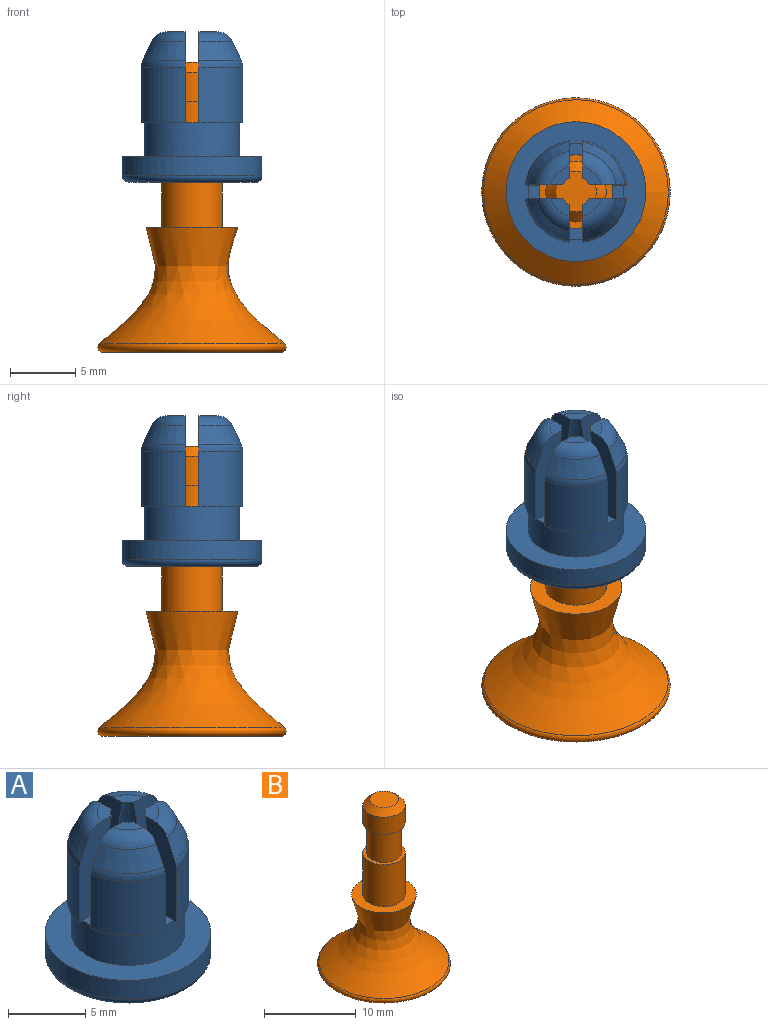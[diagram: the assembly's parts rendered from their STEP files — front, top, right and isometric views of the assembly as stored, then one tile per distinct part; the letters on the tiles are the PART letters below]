
ASSEMBLY  parts=2 mates=1
PART A: 50 faces, bbox 11.7x11.7x11.7 mm
  f0: torus R=2.67mm, axis (0,0,-1), area 2.8mm2, adj f7,f9,f12,f21
  f1: cone r=3.94mm half-angle=25.1deg, axis (0,0,-1), area 7.1mm2, adj f10,f41,f42,f47
  f2: torus R=1.99mm, axis (0,0,-1), area 4.4mm2, adj f9,f12,f14,f21
  f3: plane 1.41x1.41mm, normal (0,0,1), area 1.2mm2, adj f4,f10,f42,f47
  f4: cone r=1.82mm half-angle=9.5deg, axis (0,0,-1), area 5.1mm2, adj f3,f5,f10,f47
  f5: cone r=2.83mm half-angle=45deg, axis (0,0,-1), area 3.7mm2, adj f4,f10,f43,f47
  f6: plane 3.4x3.4mm, normal (0,0,-1), area 1.3mm2, adj f7,f9,f21,f37
  f7: cylinder r=3.94mm len=4.29mm, axis (0,0,1), area 22.2mm2, adj f0,f6,f9,f21
  f8: plane 1.02x0.9mm, normal (0,0,1), area 0.9mm2, adj f9,f10,f37,f43
  f9: plane 7.11x2.98mm, normal (0,1,0), area 12.4mm2, adj f0,f2,f6,f7,f8,f12,f14,f15
  f10: plane 7.11x2.98mm, normal (0,-1,0), area 12.4mm2, adj f1,f3,f4,f5,f8,f38,f39,f41
  f11: torus R=2.67mm, axis (0,0,-1), area 2.8mm2, adj f18,f20,f23,f32
  f12: cone r=3.94mm half-angle=25.1deg, axis (0,0,-1), area 7.1mm2, adj f0,f2,f9,f21
  f13: torus R=1.99mm, axis (0,0,-1), area 4.4mm2, adj f20,f23,f25,f32
  f14: plane 1.41x1.41mm, normal (0,0,1), area 1.2mm2, adj f2,f9,f15,f21
  f15: cone r=1.82mm half-angle=9.5deg, axis (0,0,-1), area 5.1mm2, adj f9,f14,f16,f21
  f16: cone r=2.83mm half-angle=45deg, axis (0,0,-1), area 3.7mm2, adj f9,f15,f21,f43
  f17: plane 3.4x3.4mm, normal (0,0,-1), area 1.3mm2, adj f18,f20,f32,f37
  f18: cylinder r=3.94mm len=4.29mm, axis (0,0,1), area 22.2mm2, adj f11,f17,f20,f32
  f19: plane 1.02x0.9mm, normal (0,0,1), area 0.9mm2, adj f20,f21,f37,f43
  f20: plane 7.11x2.98mm, normal (-1,0,0), area 12.4mm2, adj f11,f13,f17,f18,f19,f23,f25,f26
  f21: plane 7.11x2.98mm, normal (1,0,0), area 12.4mm2, adj f0,f2,f6,f7,f12,f14,f15,f16
  f22: torus R=2.67mm, axis (0,0,-1), area 2.8mm2, adj f29,f31,f40,f48
  f23: cone r=3.94mm half-angle=25.1deg, axis (0,0,-1), area 7.1mm2, adj f11,f13,f20,f32
  f24: torus R=1.99mm, axis (0,0,-1), area 4.4mm2, adj f31,f33,f40,f48
  f25: plane 1.41x1.41mm, normal (0,0,1), area 1.2mm2, adj f13,f20,f26,f32
  f26: cone r=1.82mm half-angle=9.5deg, axis (0,0,-1), area 5.1mm2, adj f20,f25,f27,f32
  f27: cone r=2.83mm half-angle=45deg, axis (0,0,-1), area 3.7mm2, adj f20,f26,f32,f43
  f28: plane 3.4x3.4mm, normal (0,0,-1), area 1.3mm2, adj f29,f31,f37,f48
  f29: cylinder r=3.94mm len=4.29mm, axis (0,0,1), area 22.2mm2, adj f22,f28,f31,f48
  f30: plane 1.02x0.9mm, normal (0,0,1), area 0.9mm2, adj f31,f32,f37,f43
  f31: plane 7.11x2.98mm, normal (0,-1,0), area 12.4mm2, adj f22,f24,f28,f29,f30,f33,f40,f43
  f32: plane 7.11x2.98mm, normal (0,1,0), area 12.4mm2, adj f11,f13,f17,f18,f23,f25,f26,f27
  f33: plane 1.41x1.41mm, normal (0,0,1), area 1.2mm2, adj f24,f31,f45,f48
  f34: plane 9.73x9.73mm, normal (0,0,-1), area 49.1mm2, adj f43,f49
  f35: cylinder r=5.37mm len=10.74mm, axis (0,0,1), area 51.4mm2, adj f36,f49
  f36: plane 10.74x10.74mm, normal (0,0,1), area 48.1mm2, adj f35,f37
  f37: cylinder r=3.68mm len=7.37mm, axis (0,0,1), area 58.8mm2, adj f6,f8,f17,f19,f28,f30,f36,f38
  f38: plane 3.4x3.4mm, normal (0,0,-1), area 1.3mm2, adj f10,f37,f39,f47
  f39: cylinder r=3.94mm len=4.29mm, axis (0,0,1), area 22.2mm2, adj f10,f38,f41,f47
  f40: cone r=3.94mm half-angle=25.1deg, axis (0,0,-1), area 7.1mm2, adj f22,f24,f31,f48
  f41: torus R=2.67mm, axis (0,0,-1), area 2.8mm2, adj f1,f10,f39,f47
  f42: torus R=1.99mm, axis (0,0,-1), area 4.4mm2, adj f1,f3,f10,f47
  f43: cylinder r=2.83mm len=6.56mm, axis (0,0,-1), area 108.6mm2, adj f5,f8,f9,f10,f16,f19,f20,f21
  f44: cone r=2.83mm half-angle=45deg, axis (0,0,-1), area 3.7mm2, adj f31,f43,f45,f48
  f45: cone r=1.82mm half-angle=9.5deg, axis (0,0,-1), area 5.1mm2, adj f31,f33,f44,f48
  f46: plane 1.02x0.9mm, normal (0,0,1), area 0.9mm2, adj f37,f43,f47,f48
  f47: plane 7.11x2.98mm, normal (1,0,0), area 12.4mm2, adj f1,f3,f4,f5,f38,f39,f41,f42
  f48: plane 7.11x2.98mm, normal (-1,0,0), area 12.4mm2, adj f22,f24,f28,f29,f33,f40,f43,f44
  f49: torus R=4.86mm, axis (0,0,1), area 26mm2, adj f34,f35
PART B: 11 faces, bbox 15.9x15.9x22.3 mm
  f0: bspline ~15.93x15.93mm, area 273.7mm2, adj f1,f2
  f1: plane 7.06x7.06mm, normal (0,0,1), area 22.2mm2, adj f0,f4
  f2: bspline ~14.46x14.46mm, area 42.2mm2, adj f0,f3
  f3: sphere r=12.32mm, area 161.2mm2, adj f2
  f4: cylinder r=2.32mm len=5.59mm, axis (0,0,-1), area 81.6mm2, adj f1,f5
  f5: plane 4.65x4.65mm, normal (0,0,1), area 5.7mm2, adj f4,f6
  f6: cylinder r=1.89mm len=4.06mm, axis (0,0,-1), area 48.3mm2, adj f5,f7
  f7: plane 4.65x4.65mm, normal (0,0,-1), area 5.7mm2, adj f6,f9
  f8: plane 3.12x3.12mm, normal (0,0,1), area 7.7mm2, adj f10
  f9: cylinder r=2.32mm len=4.65mm, axis (0,0,-1), area 33.4mm2, adj f7,f10
  f10: cone r=1.56mm half-angle=45deg, axis (0,0,-1), area 13.2mm2, adj f8,f9
PLACE A t=(0,0,-2.14)mm
PLACE B at identity fixed
MATE slider B.f6 <-> A.f0  axis (0,0,-1) through (0,0,17.22)mm
